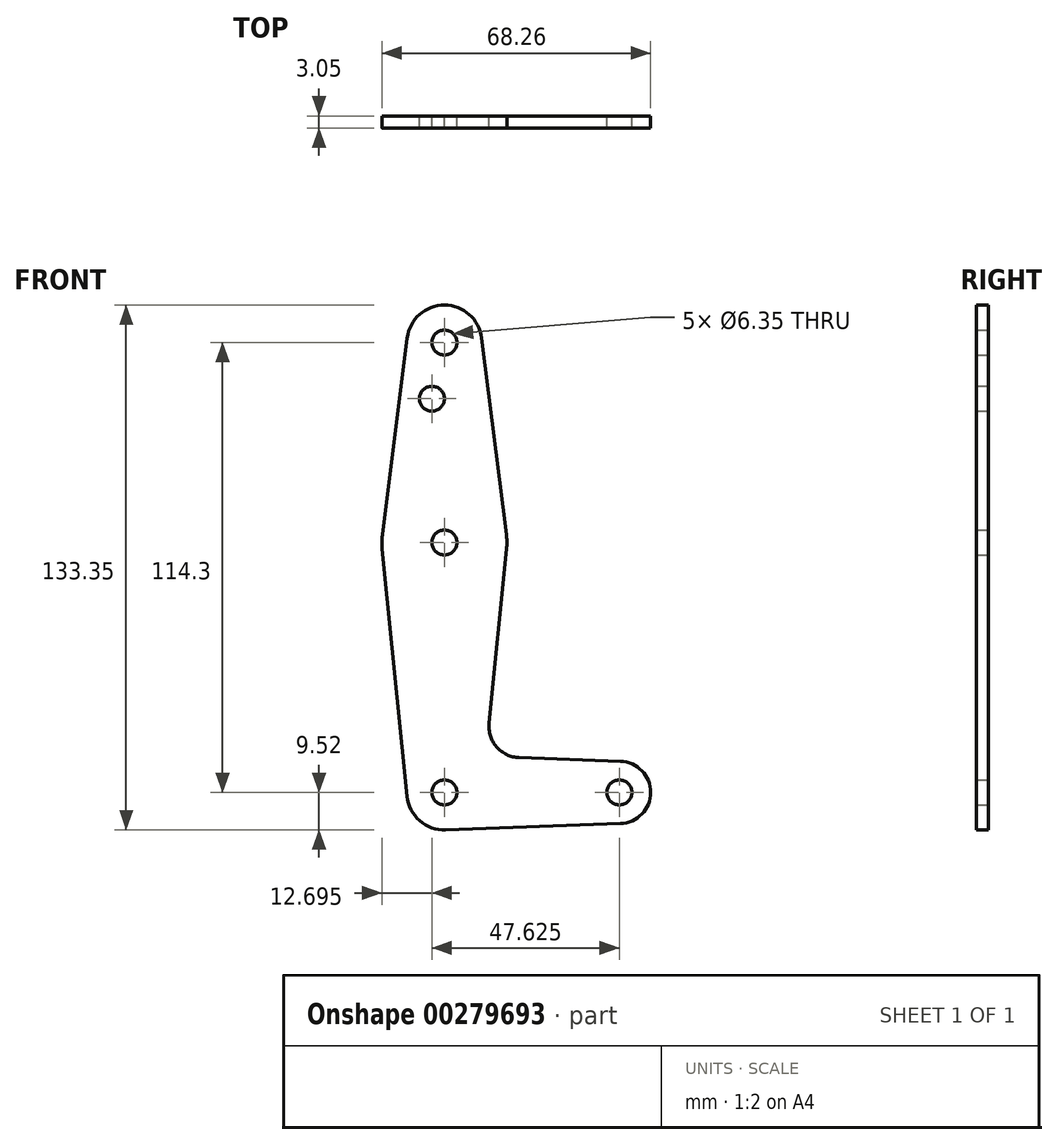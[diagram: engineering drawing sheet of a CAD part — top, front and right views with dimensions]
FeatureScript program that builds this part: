
annotation { "Feature Type Name" : "Feature", "Feature Type Description" : "" }
export const myFeature = defineFeature(function(context is Context, id is Id, definition is map)
    precondition{}
    {
        {
            var Q0;
            Q0=qCreatedBy(makeId("Front.planeOp"),FACE);
            var sketch = newSketch(context, id + "F0", { "sketchPlane" : qUnion([Q0])});
            skLineSegment(sketch, "E0", {"start": v(0, 114.3) * mm, "end": v(0, 0) * mm, "construction": true});
            skLineSegment(sketch, "E1", {"start": v(0, 0) * mm, "end": v(44.45, 0) * mm, "construction": true});
            skCircle(sketch, "E2", {"center": v(0, 114.3) * mm, "radius": 9.53 * mm});
            skCircle(sketch, "E3", {"center": v(0, 0) * mm, "radius": 9.53 * mm});
            skCircle(sketch, "E4", {"center": v(44.45, 0) * mm, "radius": 7.94 * mm});
            skCircle(sketch, "E5", {"center": v(0, 63.5) * mm, "radius": 15.88 * mm});
            skLineSegment(sketch, "E6", {"start": v(9.45, 115.5) * mm, "end": v(15.75, 65.48) * mm});
            skLineSegment(sketch, "E7", {"start": v(-15.75, 65.48) * mm, "end": v(-9.45, 115.5) * mm});
            skLineSegment(sketch, "E8", {"start": v(15.8, 61.91) * mm, "end": v(11.34, 17.6) * mm});
            skLineSegment(sketch, "E9", {"start": v(-9.48, -0.95) * mm, "end": v(-15.8, 61.91) * mm});
            skLineSegment(sketch, "E10", {"start": v(-15.8, 61.91) * mm, "end": v(-15.8, 61.91) * mm});
            skCircle(sketch, "E11", {"center": v(0, 114.3) * mm, "radius": 3.18 * mm});
            skCircle(sketch, "E12", {"center": v(0, 63.5) * mm, "radius": 3.18 * mm});
            skCircle(sketch, "E13", {"center": v(0, 0) * mm, "radius": 3.18 * mm});
            skCircle(sketch, "E14", {"center": v(44.45, 0) * mm, "radius": 3.18 * mm});
            skCircle(sketch, "E15", {"center": v(-3.17, 100.03) * mm, "radius": 3.18 * mm});
            skLineSegment(sketch, "E16", {"start": v(0.34, -9.52) * mm, "end": v(44.73, -7.93) * mm});
            skLineSegment(sketch, "E17", {"start": v(44.73, 7.93) * mm, "end": v(18.97, 8.85) * mm});
            skArc(sketch, "E18.filletArc", {"start": v(11.34, 17.6) * mm, "mid": v(13.26, 11.57) * mm, "end": v(18.97, 8.85) * mm});
            skSolve(sketch);
        }
        {
            var Q0;
            {var subQ1=sQuery(id+"F0.wireOp",EDGE,"E6");Q0=makeQuery(id+"F0.imprint","IMPRINT",FACE,{"disambiguationData":[TD([[makeQuery(id+"F0.imprint","IMPRINT",EDGE,{"derivedFrom":subQ1}),-1.0]])]});}
            var Q1;
            Q1=makeQuery(id+"F0.imprint","IMPRINT",FACE,{"disambiguationData":[TD([[makeQuery(id+"F0.imprint","IMPRINT",EDGE,{"derivedFrom":sQuery(id+"F0.wireOp",EDGE,"E11")}),-1.0]])]});
            var Q2;
            {var subQ0=sQuery(id+"F0.wireOp",EDGE,"E8");Q2=makeQuery(id+"F0.imprint","IMPRINT",FACE,{"disambiguationData":[TD([[makeQuery(id+"F0.imprint","IMPRINT",EDGE,{"derivedFrom":subQ0}),-1.0]])]});}
            var Q3;
            Q3=makeQuery(id+"F0.imprint","IMPRINT",FACE,{"disambiguationData":[TD([[makeQuery(id+"F0.imprint","IMPRINT",EDGE,{"derivedFrom":sQuery(id+"F0.wireOp",EDGE,"E12")}),-1.0]])]});
            var Q4;
            Q4=makeQuery(id+"F0.imprint","IMPRINT",FACE,{"disambiguationData":[TD([[makeQuery(id+"F0.imprint","IMPRINT",EDGE,{"derivedFrom":sQuery(id+"F0.wireOp",EDGE,"E13")}),-1.0]])]});
            var Q5;
            Q5=makeQuery(id+"F0.imprint","IMPRINT",FACE,{"disambiguationData":[TD([[makeQuery(id+"F0.imprint","IMPRINT",EDGE,{"derivedFrom":sQuery(id+"F0.wireOp",EDGE,"E14")}),-1.0]])]});
            extrude(context, id + "F1", {"entities" : qUnion([Q0, Q1, Q2, Q3, Q4, Q5]), "depth" : 3.05 * mm});
        }
    });
